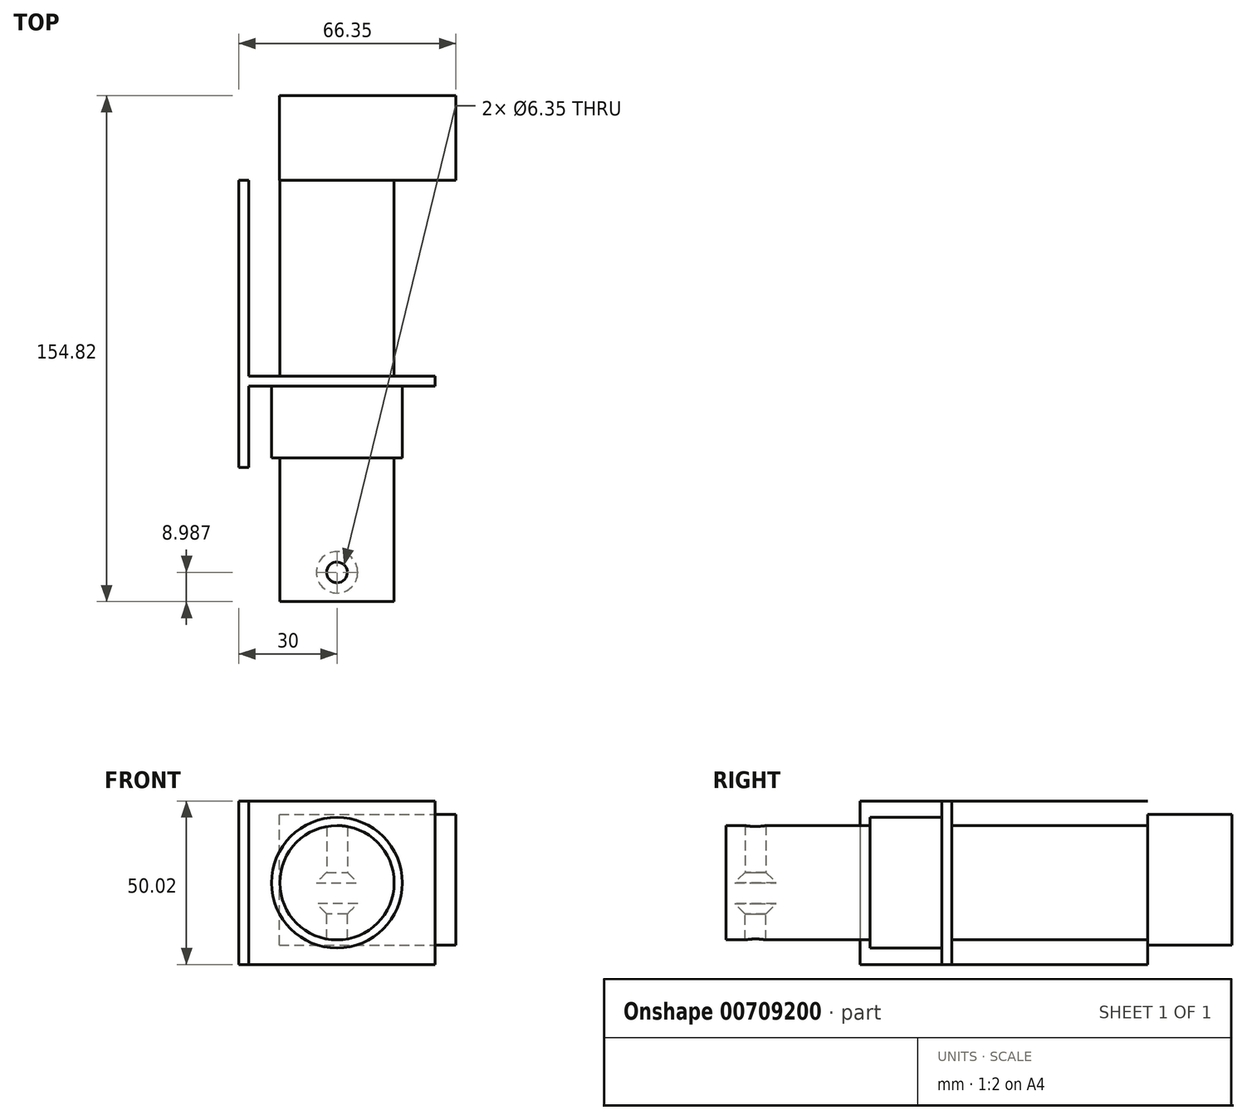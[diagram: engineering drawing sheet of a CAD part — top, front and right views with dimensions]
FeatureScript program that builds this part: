
annotation { "Feature Type Name" : "Feature", "Feature Type Description" : "" }
export const myFeature = defineFeature(function(context is Context, id is Id, definition is map)
    precondition{}
    {
        {
            var Q0;
            Q0=qCreatedBy(makeId("Front.planeOp"),FACE);
            var sketch = newSketch(context, id + "F0", { "sketchPlane" : qUnion([Q0])});
            skCircle(sketch, "E0", {"center": v(0, 0) * mm, "radius": 20 * mm});
            skSolve(sketch);
        }
        {
            var Q0;
            Q0=makeQuery(id+"F0.imprint","IMPRINT",FACE,{"disambiguationData":[TD([[makeQuery(id+"F0.imprint","IMPRINT",EDGE,{"derivedFrom":sQuery(id+"F0.wireOp",EDGE,"E0")}),1.0]])]});
            extrude(context, id + "F1", {"entities" : qUnion([Q0]), "depth" : 22.01 * mm, "offsetDistance" : 25.4 * mm});
        }
        {
            var Q0;
            Q0=makeQuery(id+"F1.opExtrude","CAP_FACE",FACE,{"disambiguationData":[OSD([sQuery(id+"F0.wireOp",EDGE,"E0")])],"isStart":false});
            var sketch = newSketch(context, id + "F2", { "sketchPlane" : qUnion([Q0])});
            skCircle(sketch, "E1", {"center": v(0, 0) * mm, "radius": 17.5 * mm});
            skSolve(sketch);
        }
        {
            var Q0;
            Q0 = qSketchRegion(id + "F2", true);
            extrude(context, id + "F3", {"entities" : qUnion([Q0]), "operationType" : NewBodyOperationType.ADD, "depth" : 44 * mm, "offsetDistance" : 25.4 * mm});
        }
        {
            var Q0;
            Q0=makeQuery(id+"F1.opExtrude","CAP_FACE",FACE,{"disambiguationData":[OSD([sQuery(id+"F0.wireOp",EDGE,"E0")])],"isStart":true});
            var sketch = newSketch(context, id + "F4", { "sketchPlane" : qUnion([Q0])});
            skLineSegment(sketch, "E2.bottom", {"start": v(-30, 25) * mm, "end": v(30, 25) * mm});
            skLineSegment(sketch, "E2.top", {"start": v(-30, -25) * mm, "end": v(30, -25) * mm});
            skLineSegment(sketch, "E2.left", {"start": v(-30, 25) * mm, "end": v(-30, -25) * mm});
            skLineSegment(sketch, "E2.right", {"start": v(30, 25) * mm, "end": v(30, -25) * mm});
            skPoint(sketch, "E2.middle", {"position": v(0, 0) * mm});
            skSolve(sketch);
        }
        {
            var Q0;
            Q0 = qSketchRegion(id + "F4", true);
            extrude(context, id + "F5", {"entities" : qUnion([Q0]), "operationType" : NewBodyOperationType.ADD, "depth" : 3 * mm, "offsetDistance" : 25.4 * mm});
        }
        {
            var Q0;
            Q0=makeQuery(id+"F5.opExtrude","CAP_FACE",FACE,{"disambiguationData":[OSD([sQuery(id+"F4.wireOp",EDGE,"E2.bottom"),sQuery(id+"F4.wireOp",EDGE,"E2.top"),sQuery(id+"F4.wireOp",EDGE,"E2.left"),sQuery(id+"F4.wireOp",EDGE,"E2.right")])],"isStart":true});
            var sketch = newSketch(context, id + "F6", { "sketchPlane" : qUnion([Q0])});
            skLineSegment(sketch, "E3.bottom", {"start": v(-27, 25) * mm, "end": v(-30, 25) * mm});
            skLineSegment(sketch, "E3.top", {"start": v(-27, -25) * mm, "end": v(-30, -25) * mm});
            skLineSegment(sketch, "E3.left", {"start": v(-27, 25) * mm, "end": v(-27, -25) * mm});
            skLineSegment(sketch, "E3.right", {"start": v(-30, 25) * mm, "end": v(-30, -25) * mm});
            skSolve(sketch);
        }
        {
            var Q0;
            Q0 = qSketchRegion(id + "F6", true);
            extrude(context, id + "F7", {"entities" : qUnion([Q0]), "operationType" : NewBodyOperationType.ADD, "depth" : 25 * mm, "offsetDistance" : 25.4 * mm});
        }
        {
            var Q0;
            Q0=makeQuery(id+"F5.opExtrude","CAP_FACE",FACE,{"disambiguationData":[OSD([sQuery(id+"F4.wireOp",EDGE,"E2.bottom"),sQuery(id+"F4.wireOp",EDGE,"E2.top"),sQuery(id+"F4.wireOp",EDGE,"E2.left"),sQuery(id+"F4.wireOp",EDGE,"E2.right")])],"isStart":false});
            var sketch = newSketch(context, id + "F8", { "sketchPlane" : qUnion([Q0])});
            skLineSegment(sketch, "E4.bottom", {"start": v(27, -25) * mm, "end": v(30, -25) * mm});
            skLineSegment(sketch, "E4.top", {"start": v(27, 25) * mm, "end": v(30, 25) * mm});
            skLineSegment(sketch, "E4.left", {"start": v(27, -25) * mm, "end": v(27, 25) * mm});
            skLineSegment(sketch, "E4.right", {"start": v(30, -25) * mm, "end": v(30, 25) * mm});
            skSolve(sketch);
        }
        {
            var Q0;
            Q0 = qSketchRegion(id + "F8", true);
            extrude(context, id + "F9", {"entities" : qUnion([Q0]), "operationType" : NewBodyOperationType.ADD, "depth" : 60 * mm, "offsetDistance" : 25.4 * mm});
        }
        {
            var Q0;
            Q0=makeQuery(id+"F5.opExtrude","CAP_FACE",FACE,{"disambiguationData":[OSD([sQuery(id+"F4.wireOp",EDGE,"E2.bottom"),sQuery(id+"F4.wireOp",EDGE,"E2.top"),sQuery(id+"F4.wireOp",EDGE,"E2.left"),sQuery(id+"F4.wireOp",EDGE,"E2.right")])],"isStart":false});
            var sketch = newSketch(context, id + "F10", { "sketchPlane" : qUnion([Q0])});
            skCircle(sketch, "E5", {"center": v(0, 0) * mm, "radius": 17.5 * mm});
            skSolve(sketch);
        }
        {
            var Q0;
            Q0 = qSketchRegion(id + "F10", true);
            extrude(context, id + "F11", {"entities" : qUnion([Q0]), "operationType" : NewBodyOperationType.ADD, "depth" : 60 * mm, "offsetDistance" : 25.4 * mm});
        }
        {
            var Q0;
            Q0=makeQuery(id+"F11.opExtrude","CAP_FACE",FACE,{"disambiguationData":[OSD([sQuery(id+"F10.wireOp",EDGE,"E5")])],"isStart":false});
            var sketch = newSketch(context, id + "F12", { "sketchPlane" : qUnion([Q0])});
            skLineSegment(sketch, "E6.bottom", {"start": v(17.65, -19.03) * mm, "end": v(-36.35, -19.03) * mm});
            skLineSegment(sketch, "E6.top", {"start": v(17.65, 20.97) * mm, "end": v(-36.35, 20.97) * mm});
            skLineSegment(sketch, "E6.left", {"start": v(17.65, -19.03) * mm, "end": v(17.65, 20.97) * mm});
            skLineSegment(sketch, "E6.right", {"start": v(-36.35, -19.03) * mm, "end": v(-36.35, 20.97) * mm});
            skSolve(sketch);
        }
        {
            var Q0;
            Q0 = qSketchRegion(id + "F12", true);
            extrude(context, id + "F13", {"entities" : qUnion([Q0]), "operationType" : NewBodyOperationType.ADD, "depth" : 25.8 * mm, "offsetDistance" : 25.4 * mm});
        }
        {
            var Q0;
            Q0=qCreatedBy(makeId("Top.planeOp"),FACE);
            var sketch = newSketch(context, id + "F14", { "sketchPlane" : qUnion([Q0])});
            skCircle(sketch, "E7", {"center": v(0, -57.03) * mm, "radius": 4.5 * mm});
            skSolve(sketch);
        }
        {
            var Q0;
            Q0=sQuery(id+"F14.wireOp",VERTEX,"E7.center");
            var Q1;
            Q1=makeQuery(id+"F1.opExtrude","SWEPT_BODY",BODY,{"disambiguationData":[OSD([sQuery(id+"F0.wireOp",EDGE,"E0")])]});
            hole(context, id + "F15", {"style" : HoleStyle.C_SINK, "endStyle" : HoleEndStyle.THROUGH, "oppositeDirection" : true, "holeDiameter" : 6.35 * mm, "cSinkDiameter" : 12.7 * mm, "cSinkAngle" : 90 * degree, "majorDiameter" : 6.35 * mm, "isTappedThrough" : true, "tappedDepth" : 12.7 * mm, "tapClearance" : 3, "locations" : qUnion([Q0]), "scope" : qUnion([Q1])});
        }
        {
            var Q0;
            Q0=qCreatedBy(makeId("Top.planeOp"),FACE);
            cPlane(context, id + "F16", {"entities" : qUnion([Q0]), "cplaneType" : CPlaneType.OFFSET, "offset" : 6.35 * mm, "oppositeDirection" : true, "width" : 152.4 * mm, "height" : 152.4 * mm});
        }
        {
            var Q0;
            Q0=qCreatedBy(id+"F16.planeOp",FACE);
            var sketch = newSketch(context, id + "F17", { "sketchPlane" : qUnion([Q0])});
            skCircle(sketch, "E8", {"center": v(0, -57.03) * mm, "radius": 3.18 * mm});
            skSolve(sketch);
        }
        {
            var Q0;
            Q0=sQuery(id+"F17.wireOp",VERTEX,"E8.center");
            var Q1;
            Q1=makeQuery(id+"F1.opExtrude","SWEPT_BODY",BODY,{"disambiguationData":[OSD([sQuery(id+"F0.wireOp",EDGE,"E0")])]});
            hole(context, id + "F18", {"style" : HoleStyle.C_SINK, "endStyle" : HoleEndStyle.THROUGH, "holeDiameter" : 6.35 * mm, "cSinkDiameter" : 12.7 * mm, "cSinkAngle" : 90 * degree, "majorDiameter" : 6.35 * mm, "isTappedThrough" : true, "tappedDepth" : 12.7 * mm, "tapClearance" : 3, "locations" : qUnion([Q0]), "scope" : qUnion([Q1])});
        }
    });
